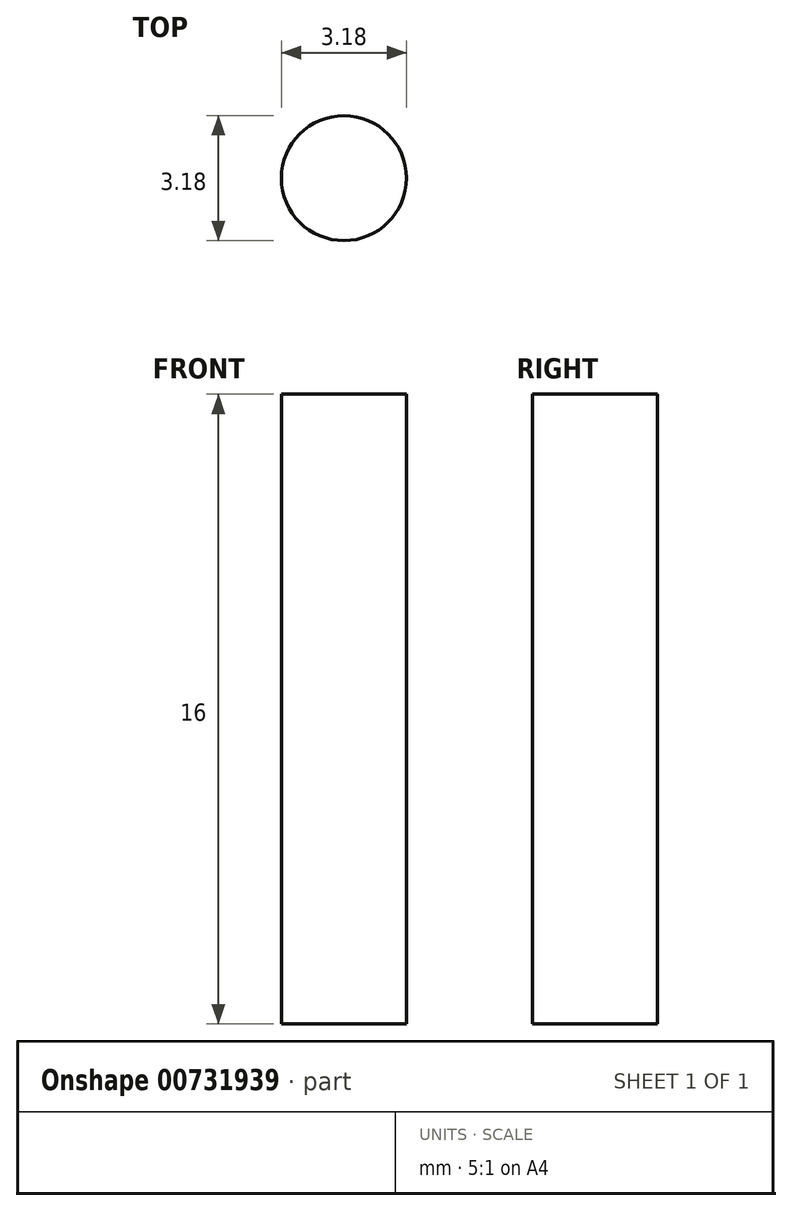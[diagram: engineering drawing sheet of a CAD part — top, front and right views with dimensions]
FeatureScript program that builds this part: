
annotation { "Feature Type Name" : "Feature", "Feature Type Description" : "" }
export const myFeature = defineFeature(function(context is Context, id is Id, definition is map)
    precondition{}
    {
        {
            var Q0;
            Q0=qCreatedBy(makeId("Top.planeOp"),FACE);
            var sketch = newSketch(context, id + "F0", { "sketchPlane" : qUnion([Q0])});
            skCircle(sketch, "E0", {"center": v(0, 0) * mm, "radius": 1.59 * mm});
            skSolve(sketch);
        }
        {
            var Q0;
            Q0=makeQuery(id+"F0.imprint","IMPRINT",FACE,{"disambiguationData":[TD([[makeQuery(id+"F0.imprint","IMPRINT",EDGE,{"derivedFrom":sQuery(id+"F0.wireOp",EDGE,"E0")}),1.0]])]});
            extrude(context, id + "F1", {"entities" : qUnion([Q0]), "depth" : 16 * mm, "offsetDistance" : 25.4 * mm});
        }
    });
